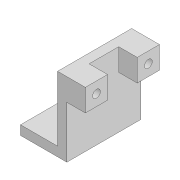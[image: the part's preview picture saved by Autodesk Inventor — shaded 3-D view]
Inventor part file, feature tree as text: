
AUTODESK INVENTOR PART (.ipt)
format: ipt  version: 2020 (Build 240168000, 168)  size: 146,944 bytes
history: native  units: mm
features: extrude x5, sketch x5, other x1
ambient origin geometry x8: Origin, YZ Plane, XZ Plane, XY Plane, X Axis, Y Axis, Z Axis, Center Point
bodies: Body1 (feature_tree)
feature tree (11):
  other  "Sólido1"
  extrude  "Extrusão1"  Depth=40.0mm
  extrude  "Extrusão2"  Depth=5.0mm
  extrude  "Extrusão3"  Depth=40.0mm TaperAngle=0.0deg
  extrude  "Extrusão4"  TaperAngle=0.0deg  [1 undecoded]
  extrude  "Extrusão5"  Depth=12.0mm
  sketch  "Esboço1"  dims[d0=25.0mm d1=40.0mm]
  sketch  "Esboço2"  dims[d2=40.0mm d3=0.0mm d4=5.0mm]
  sketch  "Esboço3"  dims[d5=5.0mm d6=40.0mm d7=0.0mm]
  sketch  "Esboço4"  dims[d8=12.0mm d9=0.0mm]
  sketch  "Esboço5"  dims[d10=0.0mm d11=12.0mm d12=12.0mm d13=4.2mm d14=4.2mm d15=10.0mm d16=0.0mm d17=6.0mm d18=6.0mm d19=6.0mm d20=6.0mm d21=50.0mm d22=0.0mm d23=6.9mm d24=6.9mm d25=6.0mm d26=0.0mm]
note: 1 required parameter value undecoded (feature->parameter linkage not recoverable at this tier; creation-order binding heuristic only, values carry confidence <= 0.55)
